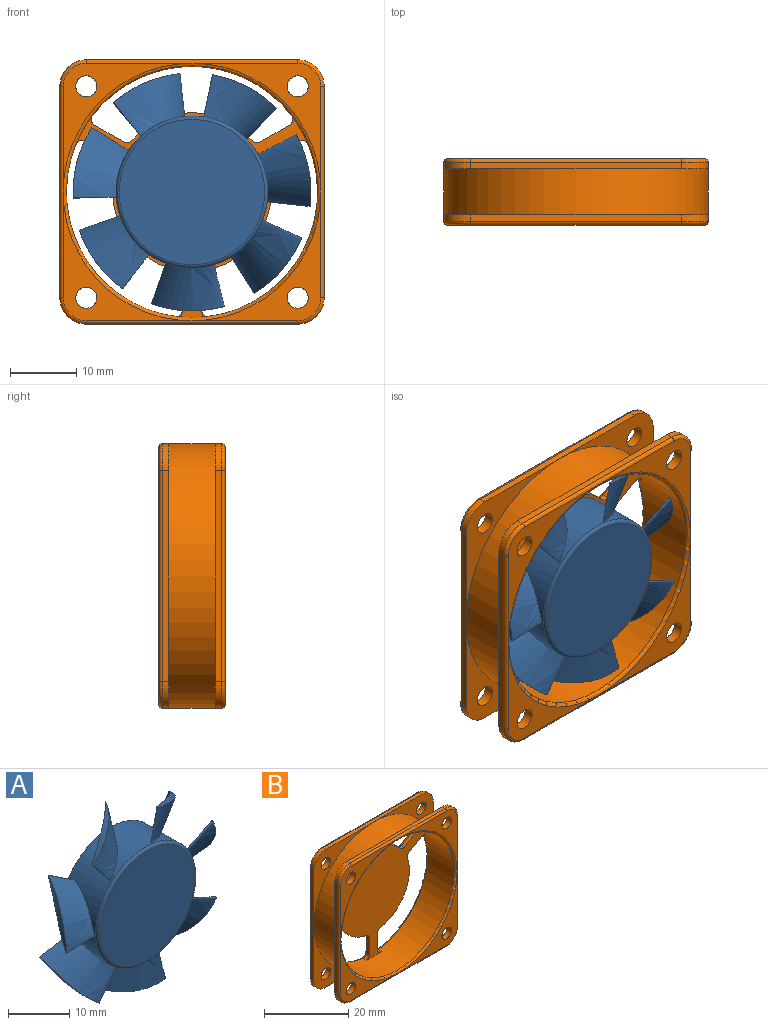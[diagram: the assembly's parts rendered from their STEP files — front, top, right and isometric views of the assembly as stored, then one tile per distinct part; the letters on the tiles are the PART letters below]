
ASSEMBLY  parts=2 mates=1
PART A: 25 faces, bbox 37.7x8.5x37 mm
  f0: bspline ~12.01x11.73mm, area 80.1mm2, adj f1,f16,f23
  f1: bspline ~11.97x11.62mm, area 74.3mm2, adj f0,f16,f23
  f2: bspline ~11.28x9.43mm, area 80.1mm2, adj f3,f16,f22
  f3: bspline ~11.15x9.02mm, area 74.3mm2, adj f2,f16,f22
  f4: bspline ~11.34x11.08mm, area 80.1mm2, adj f5,f16,f21
  f5: bspline ~11.22x11.06mm, area 74.3mm2, adj f4,f16,f21
  f6: bspline ~12.03x10.75mm, area 80.1mm2, adj f7,f16,f20
  f7: bspline ~11.98x10.69mm, area 74.3mm2, adj f6,f16,f20
  f8: bspline ~11.28x9.61mm, area 80.1mm2, adj f9,f16,f19
  f9: bspline ~11.15x9.19mm, area 74.3mm2, adj f8,f16,f19
  f10: bspline ~12.33x11.53mm, area 80.1mm2, adj f11,f16,f18
  f11: bspline ~12.1x11.2mm, area 74.3mm2, adj f10,f16,f18
  f12: bspline ~11.43x7.21mm, area 75.1mm2, adj f13,f16,f17
  f13: bspline ~11.57x7.64mm, area 80.7mm2, adj f12,f16,f17
  f14: plane 23x23mm, normal (0,1,0), area 415.5mm2, adj f16
  f15: plane 22x22mm, normal (0,-1,0), area 380.1mm2, adj f24
  f16: cylinder r=11.5mm len=23mm, axis (0,-1,0), area 539.6mm2, adj f0,f1,f2,f3,f4,f5,f6,f7
  f17: cylinder r=18mm len=11.03mm, axis (0,-1,0), area 10.3mm2, adj f12,f13
  f18: cylinder r=18mm len=8.38mm, axis (0,-1,0), area 10.3mm2, adj f10,f11
  f19: cylinder r=18mm len=10.84mm, axis (0,-1,0), area 10.3mm2, adj f8,f9
  f20: cylinder r=18mm len=9.77mm, axis (0,-1,0), area 10.3mm2, adj f6,f7
  f21: cylinder r=18mm len=10.11mm, axis (0,-1,0), area 10.3mm2, adj f4,f5
  f22: cylinder r=18mm len=10.66mm, axis (0,-1,0), area 10.3mm2, adj f2,f3
  f23: cylinder r=18mm len=8.87mm, axis (0,-1,0), area 10.3mm2, adj f0,f1
  f24: torus R=11mm, axis (0,-1,0), area 55.9mm2, adj f15,f16
PART B: 102 faces, bbox 43x10x42.8 mm
  f0: plane 19.5x19.5mm, normal (0,-1,0), area 70.9mm2, adj f85,f87,f89,f93,f99
  f1: plane 19.5x19.5mm, normal (0,-1,0), area 70.9mm2, adj f85,f86,f88,f93,f100
  f2: plane 19.5x19.5mm, normal (0,-1,0), area 70.9mm2, adj f88,f90,f92,f93,f101
  f3: cylinder r=19mm len=38mm, axis (0,-1,0), area 1059.2mm2, adj f31,f41,f42,f43,f44,f45,f46,f60
  f4: cylinder r=20mm len=40mm, axis (0,-1,0), area 879.6mm2, adj f5,f6,f7,f16,f23,f25,f28,f30
  f5: plane 20x20mm, normal (0,1,0), area 74.4mm2, adj f4,f8,f9,f10,f101
  f6: plane 20x20mm, normal (0,1,0), area 74.4mm2, adj f4,f10,f11,f12,f100
  f7: plane 20x20mm, normal (0,1,0), area 74.4mm2, adj f4,f12,f13,f14,f99
  f8: plane 32x1mm, normal (0,0,-1), area 32mm2, adj f5,f9,f15,f16,f92
  f9: cylinder r=4mm len=4mm, axis (0,-1,0), area 6.3mm2, adj f5,f8,f10,f90
  f10: plane 32x1mm, normal (1,0,0), area 32mm2, adj f5,f6,f9,f11,f88
  f11: cylinder r=4mm len=4mm, axis (0,-1,0), area 6.3mm2, adj f6,f10,f12,f86
  f12: plane 32x1mm, normal (0,0,1), area 32mm2, adj f6,f7,f11,f13,f85
  f13: cylinder r=4mm len=4mm, axis (0,-1,0), area 6.3mm2, adj f7,f12,f14,f87
  f14: plane 32x1mm, normal (-1,0,0), area 32mm2, adj f7,f13,f15,f16,f89
  f15: cylinder r=4mm len=4mm, axis (0,-1,0), area 6.3mm2, adj f8,f14,f16,f91
  f16: plane 20x20mm, normal (0,1,0), area 74.4mm2, adj f4,f8,f14,f15,f98
  f17: plane 19.5x19.5mm, normal (0,-1,0), area 70.9mm2, adj f89,f91,f92,f93,f98
  f18: plane 39x39mm, normal (0,1,0), area 748.1mm2, adj f53,f54,f55,f56,f57,f58,f59,f60
  f19: plane 32x1mm, normal (-1,0,0), area 32mm2, adj f20,f27,f28,f30,f81
  f20: cylinder r=4mm len=4mm, axis (0,1,0), area 6.3mm2, adj f19,f29,f30,f79
  f21: cylinder r=4mm len=4mm, axis (0,1,0), area 6.3mm2, adj f22,f23,f29,f78
  f22: plane 32x1mm, normal (1,0,0), area 32mm2, adj f21,f23,f24,f25,f80
  f23: plane 20x20mm, normal (0,-1,0), area 74.4mm2, adj f4,f21,f22,f29,f97
  f24: cylinder r=4mm len=4mm, axis (0,1,0), area 6.3mm2, adj f22,f25,f26,f82
  f25: plane 20x20mm, normal (0,-1,0), area 74.4mm2, adj f4,f22,f24,f26,f96
  f26: plane 32x1mm, normal (0,0,-1), area 32mm2, adj f24,f25,f27,f28,f84
  f27: cylinder r=4mm len=4mm, axis (0,1,0), area 6.3mm2, adj f19,f26,f28,f83
  f28: plane 20x20mm, normal (0,-1,0), area 74.4mm2, adj f4,f19,f26,f27,f95
  f29: plane 32x1mm, normal (0,0,1), area 32mm2, adj f20,f21,f23,f30,f77
  f30: plane 20x20mm, normal (0,-1,0), area 74.4mm2, adj f4,f19,f20,f29,f94
  f31: plane 35.15x31mm, normal (0,-1,0), area 513.8mm2, adj f3,f32,f33,f34,f35,f36,f37,f38
  f32: plane 4.38x2.53mm, normal (0.5,0,-0.87), area 5.1mm2, adj f31,f41,f47,f73
  f33: cylinder r=12mm len=15.77mm, axis (0,1,0), area 20.7mm2, adj f31,f47,f48,f69
  f34: plane 4.38x2.53mm, normal (-0.5,0,-0.87), area 5.1mm2, adj f31,f44,f50,f64
  f35: plane 5.06x1mm, normal (-1,0,0), area 5.1mm2, adj f31,f45,f49,f65
  f36: plane 4.38x2.53mm, normal (-0.5,0,0.87), area 5.1mm2, adj f31,f42,f52,f56
  f37: plane 4.38x2.53mm, normal (0.5,0,0.87), area 5.1mm2, adj f31,f43,f51,f57
  f38: cylinder r=12mm len=15.77mm, axis (0,1,0), area 20.7mm2, adj f31,f49,f50,f61
  f39: cylinder r=12mm len=18.21mm, axis (0,1,0), area 20.7mm2, adj f31,f51,f52,f53
  f40: plane 5.06x1mm, normal (1,0,0), area 5.1mm2, adj f31,f46,f48,f72
  f41: cylinder r=1mm len=1.43mm, axis (0,-1,0), area 1.7mm2, adj f3,f31,f32,f75
  f42: cylinder r=1mm len=1.48mm, axis (0,-1,0), area 1.7mm2, adj f3,f31,f36,f58
  f43: cylinder r=1mm len=1.48mm, axis (0,-1,0), area 1.7mm2, adj f3,f31,f37,f59
  f44: cylinder r=1mm len=1.43mm, axis (0,-1,0), area 1.7mm2, adj f3,f31,f34,f66
  f45: cylinder r=1mm len=1.13mm, axis (0,-1,0), area 1.7mm2, adj f3,f31,f35,f67
  f46: cylinder r=1mm len=1.13mm, axis (0,-1,0), area 1.7mm2, adj f3,f31,f40,f74
  f47: cylinder r=1mm len=1.2mm, axis (0,1,0), area 1.4mm2, adj f31,f32,f33,f71
  f48: cylinder r=1mm len=1mm, axis (0,1,0), area 1.4mm2, adj f31,f33,f40,f70
  f49: cylinder r=1mm len=1mm, axis (0,1,0), area 1.4mm2, adj f31,f35,f38,f63
  f50: cylinder r=1mm len=1.2mm, axis (0,1,0), area 1.4mm2, adj f31,f34,f38,f62
  f51: cylinder r=1mm len=1.26mm, axis (0,1,0), area 1.4mm2, adj f31,f37,f39,f55
  f52: cylinder r=1mm len=1.26mm, axis (0,1,0), area 1.4mm2, adj f31,f36,f39,f54
  f53: torus R=11.5mm, axis (0,-1,0), area 16mm2, adj f18,f39,f54,f55
  f54: torus R=1.5mm, axis (0,-1,0), area 1.3mm2, adj f18,f52,f53,f56
  f55: torus R=1.5mm, axis (0,-1,0), area 1.3mm2, adj f18,f51,f53,f57
  f56: cylinder r=0.5mm len=4.63mm, axis (-0.87,0,-0.5), area 4mm2, adj f18,f36,f54,f58
  f57: cylinder r=0.5mm len=4.63mm, axis (-0.87,0,0.5), area 4mm2, adj f18,f37,f55,f59
  f58: torus R=1.5mm, axis (0,-1,0), area 1.6mm2, adj f18,f42,f56,f60
  f59: torus R=1.5mm, axis (0,-1,0), area 1.6mm2, adj f18,f43,f57,f60
  f60: torus R=19.5mm, axis (0,-1,0), area 27.5mm2, adj f3,f18,f58,f59
  f61: torus R=11.5mm, axis (0,-1,0), area 16mm2, adj f18,f38,f62,f63
  f62: torus R=1.5mm, axis (0,-1,0), area 1.3mm2, adj f18,f50,f61,f64
  f63: torus R=1.5mm, axis (0,-1,0), area 1.3mm2, adj f18,f49,f61,f65
  f64: cylinder r=0.5mm len=4.63mm, axis (0.87,0,-0.5), area 4mm2, adj f18,f34,f62,f66
  f65: cylinder r=0.5mm len=5.06mm, axis (0,0,-1), area 4mm2, adj f18,f35,f63,f67
  f66: torus R=1.5mm, axis (0,-1,0), area 1.6mm2, adj f18,f44,f64,f68
  f67: torus R=1.5mm, axis (0,-1,0), area 1.6mm2, adj f18,f45,f65,f68
  f68: torus R=19.5mm, axis (0,-1,0), area 27.5mm2, adj f3,f18,f66,f67
  f69: torus R=11.5mm, axis (0,-1,0), area 16mm2, adj f18,f33,f70,f71
  f70: torus R=1.5mm, axis (0,-1,0), area 1.3mm2, adj f18,f48,f69,f72
  f71: torus R=1.5mm, axis (0,-1,0), area 1.3mm2, adj f18,f47,f69,f73
  f72: cylinder r=0.5mm len=5.06mm, axis (0,0,1), area 4mm2, adj f18,f40,f70,f74
  f73: cylinder r=0.5mm len=4.63mm, axis (0.87,0,0.5), area 4mm2, adj f18,f32,f71,f75
  f74: torus R=1.5mm, axis (0,-1,0), area 1.6mm2, adj f18,f46,f72,f76
  f75: torus R=1.5mm, axis (0,-1,0), area 1.6mm2, adj f18,f41,f73,f76
  f76: torus R=19.5mm, axis (0,-1,0), area 27.5mm2, adj f3,f18,f74,f75
  f77: cylinder r=0.5mm len=32mm, axis (-1,0,0), area 25.1mm2, adj f18,f29,f78,f79
  f78: torus R=3.5mm, axis (0,-1,0), area 4.7mm2, adj f18,f21,f77,f80
  f79: torus R=3.5mm, axis (0,-1,0), area 4.7mm2, adj f18,f20,f77,f81
  f80: cylinder r=0.5mm len=32mm, axis (0,0,1), area 25.1mm2, adj f18,f22,f78,f82
  f81: cylinder r=0.5mm len=32mm, axis (0,0,-1), area 25.1mm2, adj f18,f19,f79,f83
  f82: torus R=3.5mm, axis (0,-1,0), area 4.7mm2, adj f18,f24,f80,f84
  f83: torus R=3.5mm, axis (0,-1,0), area 4.7mm2, adj f18,f27,f81,f84
  f84: cylinder r=0.5mm len=32mm, axis (1,0,0), area 25.1mm2, adj f18,f26,f82,f83
  f85: cylinder r=0.5mm len=32mm, axis (-1,0,0), area 25.1mm2, adj f0,f1,f12,f86,f87
  f86: torus R=3.5mm, axis (0,-1,0), area 4.7mm2, adj f1,f11,f85,f88
  f87: torus R=3.5mm, axis (0,-1,0), area 4.7mm2, adj f0,f13,f85,f89
  f88: cylinder r=0.5mm len=32mm, axis (0,0,1), area 25.1mm2, adj f1,f2,f10,f86,f90
  f89: cylinder r=0.5mm len=32mm, axis (0,0,-1), area 25.1mm2, adj f0,f14,f17,f87,f91
  f90: torus R=3.5mm, axis (0,-1,0), area 4.7mm2, adj f2,f9,f88,f92
  f91: torus R=3.5mm, axis (0,-1,0), area 4.7mm2, adj f15,f17,f89,f92
  f92: cylinder r=0.5mm len=32mm, axis (1,0,0), area 25.1mm2, adj f2,f8,f17,f90,f91
  f93: torus R=19.5mm, axis (0,-1,0), area 94.7mm2, adj f0,f1,f2,f3,f17
  f94: cylinder r=1.6mm len=3.2mm, axis (0,-1,0), area 15.1mm2, adj f18,f30
  f95: cylinder r=1.6mm len=3.2mm, axis (0,-1,0), area 15.1mm2, adj f18,f28
  f96: cylinder r=1.6mm len=3.2mm, axis (0,-1,0), area 15.1mm2, adj f18,f25
  f97: cylinder r=1.6mm len=3.2mm, axis (0,-1,0), area 15.1mm2, adj f18,f23
  f98: cylinder r=1.6mm len=3.2mm, axis (0,-1,0), area 15.1mm2, adj f16,f17
  f99: cylinder r=1.6mm len=3.2mm, axis (0,-1,0), area 15.1mm2, adj f0,f7
  f100: cylinder r=1.6mm len=3.2mm, axis (0,-1,0), area 15.1mm2, adj f1,f6
  f101: cylinder r=1.6mm len=3.2mm, axis (0,-1,0), area 15.1mm2, adj f2,f5
PLACE A at identity
PLACE B at identity fixed
MATE revolute B.f3 <-> A.f16  axis (0,-1,0) through (0,8.5,0)mm
